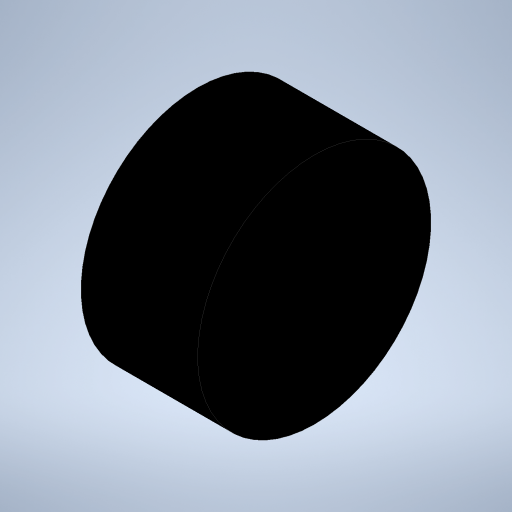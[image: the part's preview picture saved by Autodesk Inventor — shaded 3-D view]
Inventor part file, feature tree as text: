
AUTODESK INVENTOR PART (.ipt)
format: ipt  version: 2023 (Build 270158000, 158)  size: 198,144 bytes
history: native  units: in
note: dims shown in document units (in); Inventor stores cm internally (conversion verified against a paired STEP export)
features: extrude x1, sketch x1
ambient origin geometry x8: Origin, YZ Plane, XZ Plane, XY Plane, X Axis, Y Axis, Z Axis, Center Point
bodies: Solid1 (feature_tree)
feature tree (2):
  extrude  "Extrusion1"  Depth=0.0394in TaperAngle=0.0deg
  sketch  "Sketch1"  dims[d0=0.0787in d1=0.0394in d2=0.0in]
